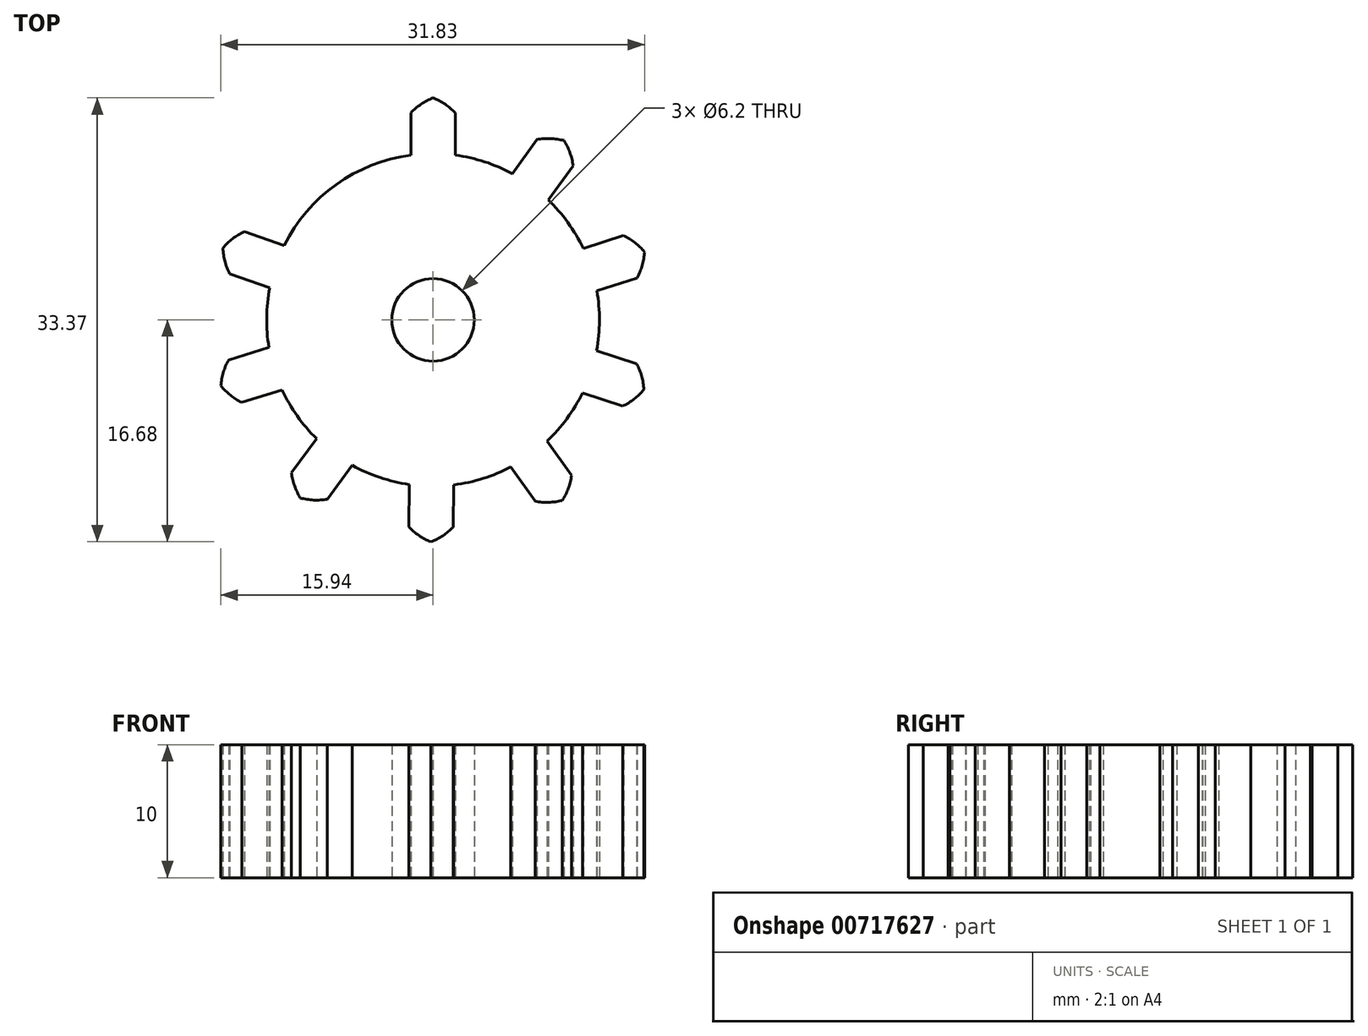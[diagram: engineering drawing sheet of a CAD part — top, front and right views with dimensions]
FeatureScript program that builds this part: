
annotation { "Feature Type Name" : "Feature", "Feature Type Description" : "" }
export const myFeature = defineFeature(function(context is Context, id is Id, definition is map)
    precondition{}
    {
        {
            var Q0;
            Q0=qCreatedBy(makeId("Top.planeOp"),FACE);
            var sketch = newSketch(context, id + "F0", { "sketchPlane" : qUnion([Q0])});
            skCircle(sketch, "E0", {"center": v(0, 0) * mm, "radius": 3.1 * mm});
            skArc(sketch, "E1", {"start": v(-1.67, 12.39) * mm, "mid": v(0, -12.5) * mm, "end": v(1.67, 12.39) * mm});
            skPoint(sketch, "E2.middle", {"position": v(0, 12.5) * mm});
            skArc(sketch, "E3", {"start": v(0, 16.69) * mm, "mid": v(-0.9, 16.22) * mm, "end": v(-1.67, 15.56) * mm});
            skArc(sketch, "E4.trimOffspring", {"start": v(1.67, 15.56) * mm, "mid": v(0.9, 16.22) * mm, "end": v(0, 16.69) * mm});
            skLineSegment(sketch, "E5.trimOffspring", {"start": v(-1.67, 12.39) * mm, "end": v(-1.67, 15.56) * mm});
            skLineSegment(sketch, "E6.trimOffspring", {"start": v(1.67, 12.39) * mm, "end": v(1.67, 15.56) * mm});
            skLineSegment(sketch, "E7.1.0", {"start": v(5.95, 11) * mm, "end": v(7.82, 13.56) * mm});
            skArc(sketch, "E7.1.1", {"start": v(9.83, 13.48) * mm, "mid": v(8.83, 13.63) * mm, "end": v(7.82, 13.56) * mm});
            skArc(sketch, "E7.1.2", {"start": v(10.52, 11.58) * mm, "mid": v(10.28, 12.57) * mm, "end": v(9.83, 13.48) * mm});
            skLineSegment(sketch, "E7.1.3", {"start": v(8.65, 9.02) * mm, "end": v(10.52, 11.58) * mm});
            skArc(sketch, "E7.1.4", {"start": v(5.95, 11) * mm, "mid": v(-7.37, -10.1) * mm, "end": v(8.65, 9.02) * mm});
            skLineSegment(sketch, "E7.2.0", {"start": v(11.28, 5.38) * mm, "end": v(14.3, 6.34) * mm});
            skArc(sketch, "E7.2.1", {"start": v(15.89, 5.1) * mm, "mid": v(15.17, 5.8) * mm, "end": v(14.3, 6.34) * mm});
            skArc(sketch, "E7.2.2", {"start": v(15.33, 3.16) * mm, "mid": v(15.72, 4.1) * mm, "end": v(15.89, 5.1) * mm});
            skLineSegment(sketch, "E7.2.3", {"start": v(12.3, 2.19) * mm, "end": v(15.33, 3.16) * mm});
            skArc(sketch, "E7.2.4", {"start": v(11.28, 5.38) * mm, "mid": v(-11.9, -3.82) * mm, "end": v(12.3, 2.19) * mm});
            skLineSegment(sketch, "E7.3.0", {"start": v(12.29, -2.3) * mm, "end": v(15.3, -3.3) * mm});
            skArc(sketch, "E7.3.1", {"start": v(15.84, -5.25) * mm, "mid": v(15.68, -4.25) * mm, "end": v(15.3, -3.3) * mm});
            skArc(sketch, "E7.3.2", {"start": v(14.24, -6.48) * mm, "mid": v(15.1, -5.95) * mm, "end": v(15.84, -5.25) * mm});
            skLineSegment(sketch, "E7.3.3", {"start": v(11.23, -5.49) * mm, "end": v(14.24, -6.48) * mm});
            skArc(sketch, "E7.3.4", {"start": v(12.29, -2.3) * mm, "mid": v(-11.87, 3.93) * mm, "end": v(11.23, -5.49) * mm});
            skLineSegment(sketch, "E7.4.0", {"start": v(8.57, -9.1) * mm, "end": v(10.41, -11.69) * mm});
            skArc(sketch, "E7.4.1", {"start": v(9.7, -13.57) * mm, "mid": v(10.16, -12.67) * mm, "end": v(10.41, -11.69) * mm});
            skArc(sketch, "E7.4.2", {"start": v(7.69, -13.63) * mm, "mid": v(8.7, -13.72) * mm, "end": v(9.7, -13.57) * mm});
            skLineSegment(sketch, "E7.4.3", {"start": v(5.84, -11.05) * mm, "end": v(7.69, -13.63) * mm});
            skArc(sketch, "E7.4.4", {"start": v(8.57, -9.1) * mm, "mid": v(-7.27, 10.17) * mm, "end": v(5.84, -11.05) * mm});
            skLineSegment(sketch, "E7.5.0", {"start": v(1.55, -12.4) * mm, "end": v(1.52, -15.58) * mm});
            skArc(sketch, "E7.5.1", {"start": v(-0.16, -16.68) * mm, "mid": v(0.74, -16.22) * mm, "end": v(1.52, -15.58) * mm});
            skArc(sketch, "E7.5.2", {"start": v(-1.82, -15.54) * mm, "mid": v(-1.06, -16.2) * mm, "end": v(-0.16, -16.68) * mm});
            skLineSegment(sketch, "E7.5.3", {"start": v(-1.8, -12.37) * mm, "end": v(-1.82, -15.54) * mm});
            skArc(sketch, "E7.5.4", {"start": v(1.55, -12.4) * mm, "mid": v(0.12, 12.5) * mm, "end": v(-1.8, -12.37) * mm});
            skLineSegment(sketch, "E7.6.0", {"start": v(-6.05, -10.94) * mm, "end": v(-7.95, -13.48) * mm});
            skArc(sketch, "E7.6.1", {"start": v(-9.96, -13.38) * mm, "mid": v(-8.96, -13.54) * mm, "end": v(-7.95, -13.48) * mm});
            skArc(sketch, "E7.6.2", {"start": v(-10.63, -11.48) * mm, "mid": v(-10.4, -12.47) * mm, "end": v(-9.96, -13.38) * mm});
            skLineSegment(sketch, "E7.6.3", {"start": v(-8.74, -8.94) * mm, "end": v(-10.63, -11.48) * mm});
            skArc(sketch, "E7.6.4", {"start": v(-6.05, -10.94) * mm, "mid": v(7.46, 10.03) * mm, "end": v(-8.74, -8.94) * mm});
            skLineSegment(sketch, "E7.7.0", {"start": v(-11.34, -5.27) * mm, "end": v(-14.37, -6.2) * mm});
            skArc(sketch, "E7.7.1", {"start": v(-15.94, -4.94) * mm, "mid": v(-15.22, -5.66) * mm, "end": v(-14.37, -6.2) * mm});
            skArc(sketch, "E7.7.2", {"start": v(-15.36, -3) * mm, "mid": v(-15.75, -3.94) * mm, "end": v(-15.94, -4.94) * mm});
            skLineSegment(sketch, "E7.7.3", {"start": v(-12.33, -2.07) * mm, "end": v(-15.36, -3) * mm});
            skArc(sketch, "E7.7.4", {"start": v(-11.34, -5.27) * mm, "mid": v(11.94, 3.7) * mm, "end": v(-12.33, -2.07) * mm});
            skLineSegment(sketch, "E7.8.0", {"start": v(-12.26, 2.43) * mm, "end": v(-15.26, 3.45) * mm});
            skArc(sketch, "E7.8.1", {"start": v(-15.79, 5.4) * mm, "mid": v(-15.63, 4.4) * mm, "end": v(-15.26, 3.45) * mm});
            skArc(sketch, "E7.8.2", {"start": v(-14.18, 6.62) * mm, "mid": v(-15.05, 6.1) * mm, "end": v(-15.79, 5.4) * mm});
            skLineSegment(sketch, "E7.8.3", {"start": v(-11.18, 5.6) * mm, "end": v(-14.18, 6.62) * mm});
            skArc(sketch, "E7.8.4", {"start": v(-12.26, 2.43) * mm, "mid": v(11.83, -4.05) * mm, "end": v(-11.18, 5.6) * mm});
            skLineSegment(sketch, "E7.9.0", {"start": v(-8.48, 9.19) * mm, "end": v(-10.3, 11.79) * mm});
            skArc(sketch, "E7.9.1", {"start": v(-9.57, 13.67) * mm, "mid": v(-10.04, 12.77) * mm, "end": v(-10.3, 11.79) * mm});
            skArc(sketch, "E7.9.2", {"start": v(-7.55, 13.7) * mm, "mid": v(-8.56, 13.8) * mm, "end": v(-9.57, 13.67) * mm});
            skLineSegment(sketch, "E7.9.3", {"start": v(-5.73, 11.1) * mm, "end": v(-7.55, 13.7) * mm});
            skArc(sketch, "E7.9.4", {"start": v(-8.48, 9.19) * mm, "mid": v(7.17, -10.24) * mm, "end": v(-5.73, 11.1) * mm});
            skLineSegment(sketch, "E7.anchor1", {"start": v(0, 0) * mm, "end": v(-1.67, 12.39) * mm, "construction": true});
            skLineSegment(sketch, "E7.anchor2", {"start": v(0, 0) * mm, "end": v(-8.48, 9.19) * mm, "construction": true});
            skSolve(sketch);
        }
        {
            var Q0;
            Q0=makeQuery(id+"F0.imprint","IMPRINT",FACE,{"disambiguationData":[TD([[makeQuery(id+"F0.imprint","IMPRINT",EDGE,{"derivedFrom":sQuery(id+"F0.wireOp",EDGE,"E0")}),-1.0]])]});
            var Q1;
            {var subQ1=sQuery(id+"F0.wireOp",EDGE,"E7.8.0");Q1=makeQuery(id+"F0.imprint","IMPRINT",FACE,{"disambiguationData":[TD([[makeQuery(id+"F0.imprint","IMPRINT",EDGE,{"derivedFrom":subQ1}),-1.0]])]});}
            var Q2;
            Q2=makeQuery(id+"F0.imprint","IMPRINT",FACE,{"disambiguationData":[TD([[makeQuery(id+"F0.imprint","IMPRINT",EDGE,{"derivedFrom":sQuery(id+"F0.wireOp",EDGE,"E7.8.4")}),-1.0]])]});
            var Q3;
            Q3=makeQuery(id+"F0.imprint","IMPRINT",FACE,{"disambiguationData":[TD([[makeQuery(id+"F0.imprint","IMPRINT",EDGE,{"derivedFrom":sQuery(id+"F0.wireOp",EDGE,"E3")}),1.0]])]});
            var Q4;
            {var subQ1=sQuery(id+"F0.wireOp",EDGE,"E7.1.0");Q4=makeQuery(id+"F0.imprint","IMPRINT",FACE,{"disambiguationData":[TD([[makeQuery(id+"F0.imprint","IMPRINT",EDGE,{"derivedFrom":subQ1}),-1.0]])]});}
            var Q5;
            {var subQ2=sQuery(id+"F0.wireOp",EDGE,"E7.2.0");Q5=makeQuery(id+"F0.imprint","IMPRINT",FACE,{"disambiguationData":[TD([[makeQuery(id+"F0.imprint","IMPRINT",EDGE,{"derivedFrom":subQ2}),-1.0]])]});}
            var Q6;
            {var subQ1=sQuery(id+"F0.wireOp",EDGE,"E7.3.0");Q6=makeQuery(id+"F0.imprint","IMPRINT",FACE,{"disambiguationData":[TD([[makeQuery(id+"F0.imprint","IMPRINT",EDGE,{"derivedFrom":subQ1}),-1.0]])]});}
            var Q7;
            {var subQ2=sQuery(id+"F0.wireOp",EDGE,"E7.4.0");Q7=makeQuery(id+"F0.imprint","IMPRINT",FACE,{"disambiguationData":[TD([[makeQuery(id+"F0.imprint","IMPRINT",EDGE,{"derivedFrom":subQ2}),-1.0]])]});}
            var Q8;
            {var subQ1=sQuery(id+"F0.wireOp",EDGE,"E7.5.0");Q8=makeQuery(id+"F0.imprint","IMPRINT",FACE,{"disambiguationData":[TD([[makeQuery(id+"F0.imprint","IMPRINT",EDGE,{"derivedFrom":subQ1}),-1.0]])]});}
            var Q9;
            {var subQ1=sQuery(id+"F0.wireOp",EDGE,"E7.6.0");Q9=makeQuery(id+"F0.imprint","IMPRINT",FACE,{"disambiguationData":[TD([[makeQuery(id+"F0.imprint","IMPRINT",EDGE,{"derivedFrom":subQ1}),-1.0]])]});}
            var Q10;
            {var subQ1=sQuery(id+"F0.wireOp",EDGE,"E7.7.0");Q10=makeQuery(id+"F0.imprint","IMPRINT",FACE,{"disambiguationData":[TD([[makeQuery(id+"F0.imprint","IMPRINT",EDGE,{"derivedFrom":subQ1}),-1.0]])]});}
            extrude(context, id + "F1", {"entities" : qUnion([Q0, Q1, Q2, Q3, Q4, Q5, Q6, Q7, Q8, Q9, Q10]), "depth" : 10 * mm, "offsetDistance" : 25 * mm});
        }
    });
